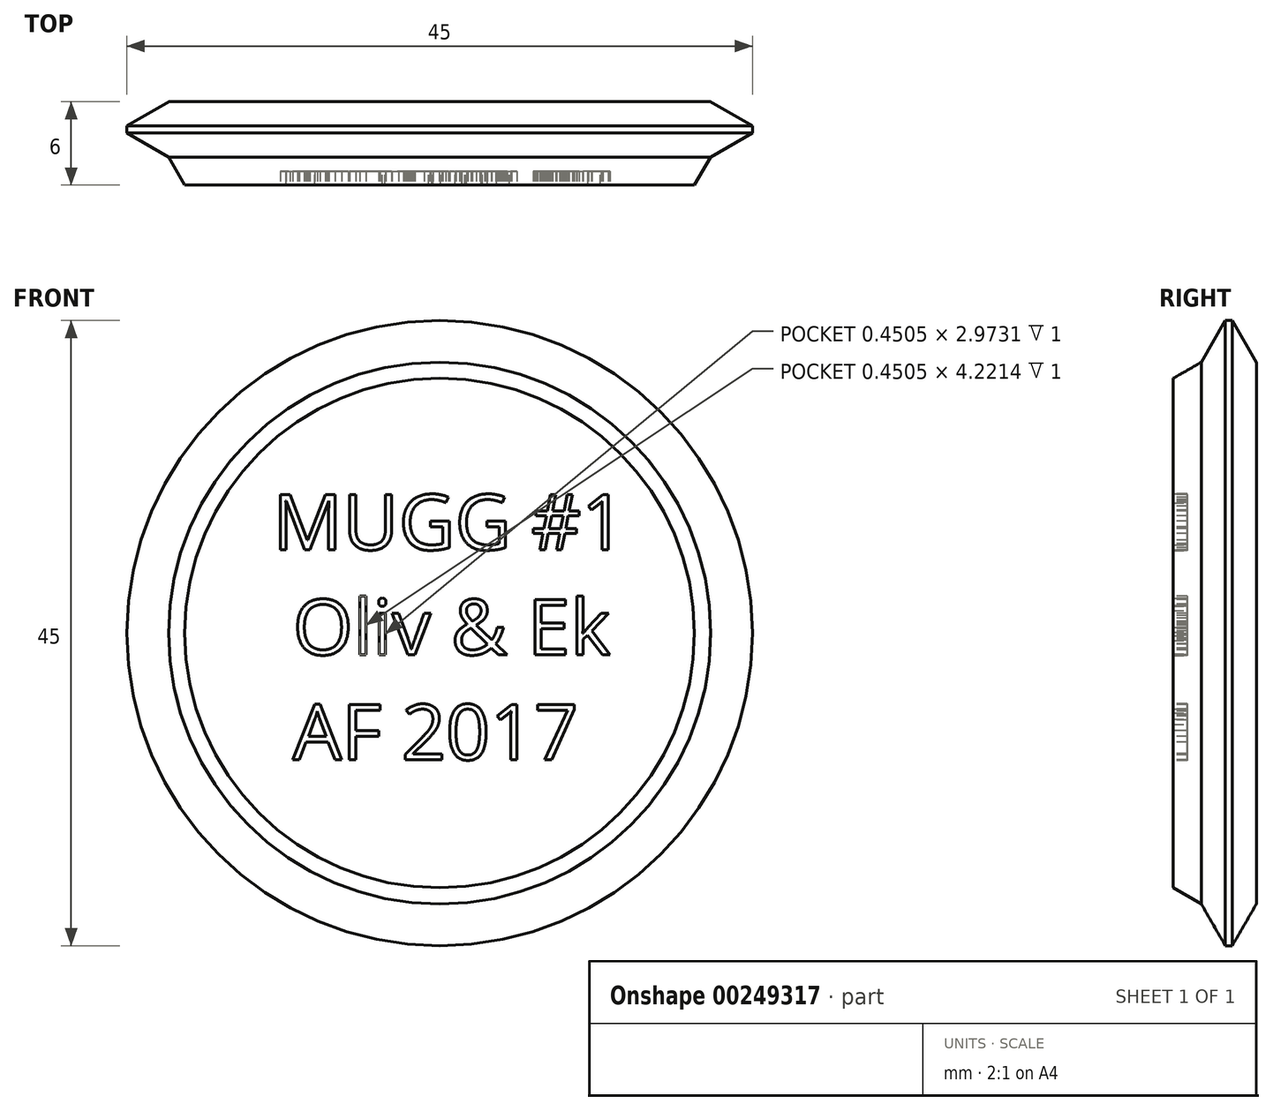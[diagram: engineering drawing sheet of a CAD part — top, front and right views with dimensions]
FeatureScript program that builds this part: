
annotation { "Feature Type Name" : "Feature", "Feature Type Description" : "" }
export const myFeature = defineFeature(function(context is Context, id is Id, definition is map)
    precondition{}
    {
        {
            var Q0;
            Q0=qCreatedBy(makeId("Front.planeOp"),FACE);
            var sketch = newSketch(context, id + "F0", { "sketchPlane" : qUnion([Q0])});
            skCircle(sketch, "E0", {"center": v(0, 0) * mm, "radius": 22.5 * mm});
            skSolve(sketch);
        }
        {
            var Q0;
            Q0=makeQuery(id+"F0.imprint","IMPRINT",FACE,{"disambiguationData":[TD([[makeQuery(id+"F0.imprint","IMPRINT",EDGE,{"derivedFrom":sQuery(id+"F0.wireOp",EDGE,"E0")}),1.0]])]});
            extrude(context, id + "F1", {"entities" : qUnion([Q0]), "depth" : 6 * mm});
        }
        {
            var Q0;
            Q0=makeQuery(id+"F1.opExtrude","CAP_EDGE",EDGE,{"disambiguationData":[OSD([sQuery(id+"F0.wireOp",EDGE,"E0")])],"isStart":false});
            chamfer(context, id + "F2", {"entities" : qUnion([Q0]), "chamferType" : ChamferType.OFFSET_ANGLE, "width" : 3.75 * mm, "oppositeDirection" : true, "angle" : 60 * degree, "tangentPropagation" : true});
        }
        {
            var Q0;
            Q0=makeQuery(id+"F1.opExtrude","CAP_FACE",FACE,{"disambiguationData":[OSD([sQuery(id+"F0.wireOp",EDGE,"E0")])],"isStart":true});
            chamfer(context, id + "F3", {"entities" : qUnion([Q0]), "chamferType" : ChamferType.OFFSET_ANGLE, "width" : 1.75 * mm, "oppositeDirection" : false, "angle" : 60 * degree, "tangentPropagation" : true});
        }
        {
            var Q0;
            Q0=qCreatedBy(makeId("Right.planeOp"),FACE);
            var sketch = newSketch(context, id + "F4", { "sketchPlane" : qUnion([Q0])});
            skLineSegment(sketch, "E1", {"start": v(-6, 16) * mm, "end": v(-2.25, 22.5) * mm, "construction": true});
            skLineSegment(sketch, "E2", {"start": v(-6, 16) * mm, "end": v(-6, 18.33) * mm});
            skLineSegment(sketch, "E3", {"start": v(-6, 16) * mm, "end": v(-3.98, 19.5) * mm});
            skLineSegment(sketch, "E4", {"start": v(6.26, 0) * mm, "end": v(-12.23, 0) * mm});
            skLineSegment(sketch, "E5", {"start": v(-3.98, 19.5) * mm, "end": v(-6, 18.33) * mm});
            skSolve(sketch);
        }
        {
            var Q0;
            Q0=makeQuery(id+"F4.imprint","IMPRINT",FACE,{"disambiguationData":[TD([[makeQuery(id+"F4.imprint","IMPRINT",EDGE,{"derivedFrom":sQuery(id+"F4.wireOp",EDGE,"4yHqjvry-Ar0T-qde3-Vb3m-68XVGBhB37GW")}),1.0]])]});
            var Q1;
            Q1=makeQuery(id+"F4.imprint","IMPRINT",FACE,{"disambiguationData":[TD([[makeQuery(id+"F4.imprint","IMPRINT",EDGE,{"derivedFrom":sQuery(id+"F4.wireOp",EDGE,"E2")}),-1.0]])]});
            var Q2;
            Q2=sQuery(id+"F4.wireOp",EDGE,"E4");
            revolve(context, id + "F5", {"operationType" : NewBodyOperationType.ADD, "entities" : qUnion([Q0, Q1]), "axis" : qUnion([Q2]), "revolveType" : RevolveType.FULL});
        }
        {
            var Q0;
            Q0=makeQuery(id+"F5.boolean.opBoolean","MERGE",FACE,{"derivedFrom":[makeQuery(id+"F1.opExtrude","CAP_FACE",FACE,{"disambiguationData":[OSD([sQuery(id+"F0.wireOp",EDGE,"E0")])],"isStart":false}),makeQuery(id+"F5.opRevolve","SWEPT_FACE",FACE,{"disambiguationData":[OSD([sQuery(id+"F4.wireOp",EDGE,"E2")])]})]});
            var sketch = newSketch(context, id + "F6", { "sketchPlane" : qUnion([Q0])});
            skText(sketch, "E6", { "text": "MUGG #1\n Oliv & Ek\n AF 2017", "fontName": "OpenSans-Regular.ttf"});
            const initialGuessF6  = {"E6": [-0.012, 0.006, 1, 0, 0.004]};
            skSetInitialGuess(sketch, initialGuessF6);
            skSolve(sketch);
        }
        {
            var Q0;
            Q0 = qSketchRegion(id + "F6", true);
            extrude(context, id + "F7", {"entities" : qUnion([Q0]), "operationType" : NewBodyOperationType.REMOVE, "oppositeDirection" : true, "depth" : 1 * mm, "offsetDistance" : 25 * mm});
        }
    });
